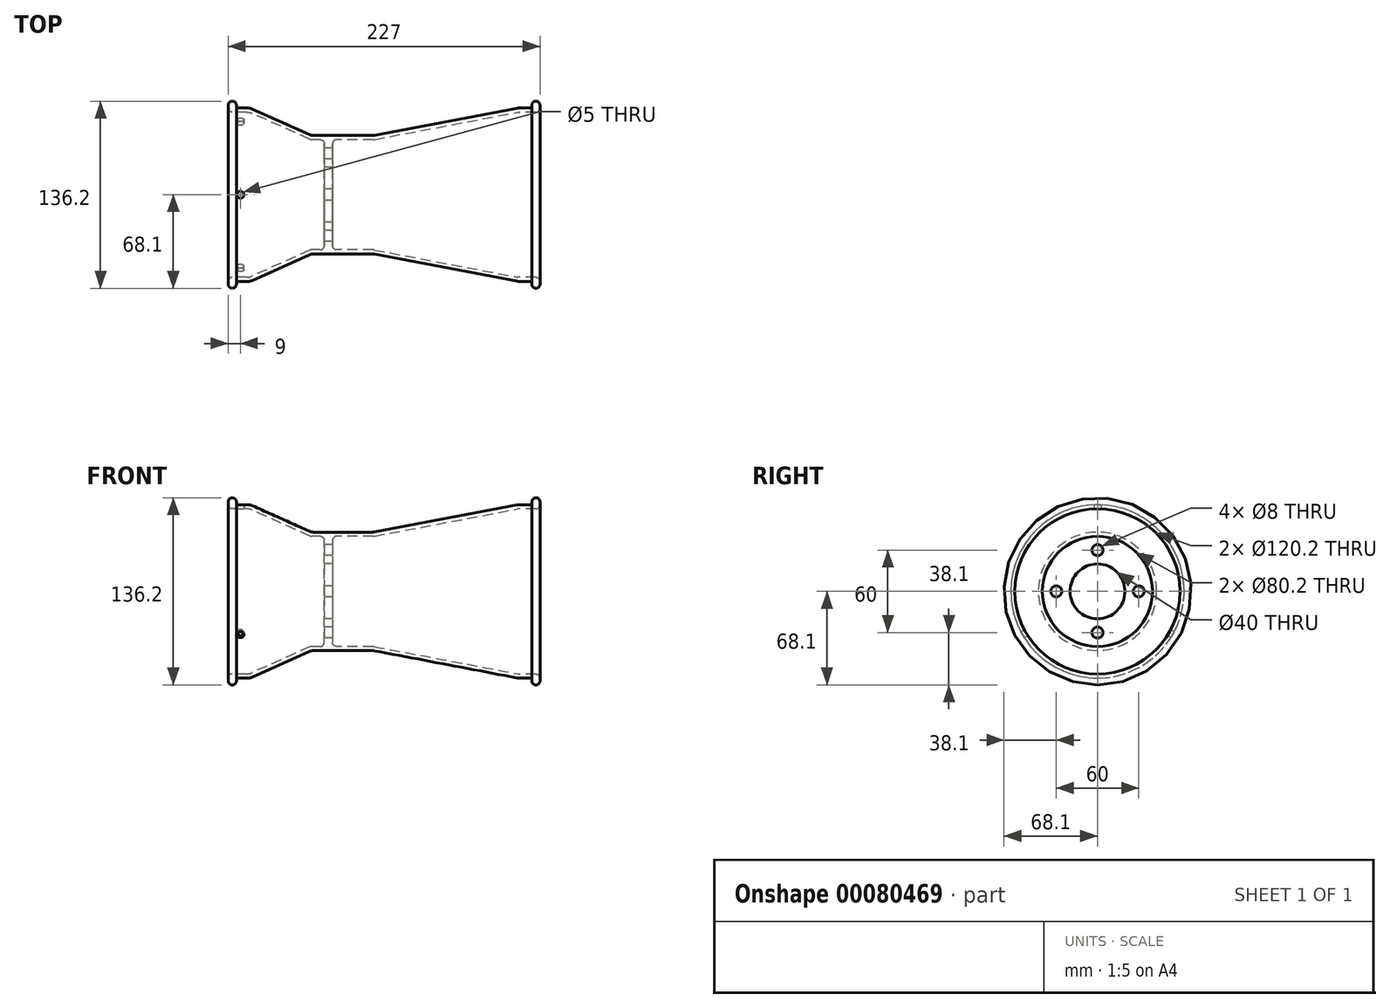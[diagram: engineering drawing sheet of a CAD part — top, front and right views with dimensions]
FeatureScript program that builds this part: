
annotation { "Feature Type Name" : "Feature", "Feature Type Description" : "" }
export const myFeature = defineFeature(function(context is Context, id is Id, definition is map)
    precondition{}
    {
        {
            var Q0;
            Q0=qCreatedBy(makeId("Front.planeOp"),FACE);
            var sketch = newSketch(context, id + "F0", { "sketchPlane" : qUnion([Q0])});
            skLineSegment(sketch, "E0", {"start": v(0, 0) * mm, "end": v(198.62, 0) * mm, "construction": true});
            skLineSegment(sketch, "E1", {"start": v(0, 68.1) * mm, "end": v(0, 60.1) * mm});
            skLineSegment(sketch, "E2", {"start": v(0, 60.1) * mm, "end": v(15.36, 60.1) * mm});
            skLineSegment(sketch, "E3", {"start": v(15.36, 60.1) * mm, "end": v(60, 40.1) * mm});
            skLineSegment(sketch, "E4", {"start": v(60, 40.1) * mm, "end": v(70, 40.1) * mm});
            skLineSegment(sketch, "E5", {"start": v(70, 40.1) * mm, "end": v(70, 0) * mm});
            skLineSegment(sketch, "E6", {"start": v(70, 0) * mm, "end": v(76, 0) * mm});
            skLineSegment(sketch, "E7", {"start": v(76, 0) * mm, "end": v(76, 40.1) * mm});
            skLineSegment(sketch, "E8", {"start": v(76, 40.1) * mm, "end": v(106, 40.1) * mm});
            skLineSegment(sketch, "E9", {"start": v(106, 40.1) * mm, "end": v(211.28, 60.1) * mm});
            skLineSegment(sketch, "E10", {"start": v(211.28, 60.1) * mm, "end": v(227, 60.1) * mm});
            skLineSegment(sketch, "E11", {"start": v(227, 60.1) * mm, "end": v(227, 68.1) * mm});
            skLineSegment(sketch, "E12", {"start": v(227, 68.1) * mm, "end": v(221, 68.1) * mm});
            skLineSegment(sketch, "E13", {"start": v(221, 68.1) * mm, "end": v(221, 63.1) * mm});
            skLineSegment(sketch, "E14", {"start": v(221, 63.1) * mm, "end": v(211, 63.1) * mm});
            skLineSegment(sketch, "E15", {"start": v(211, 63.1) * mm, "end": v(105.72, 43.1) * mm});
            skLineSegment(sketch, "E16", {"start": v(105.72, 43.1) * mm, "end": v(60.64, 43.1) * mm});
            skLineSegment(sketch, "E17", {"start": v(60.64, 43.1) * mm, "end": v(16, 63.1) * mm});
            skLineSegment(sketch, "E18", {"start": v(16, 63.1) * mm, "end": v(6, 63.1) * mm});
            skLineSegment(sketch, "E19", {"start": v(6, 63.1) * mm, "end": v(6, 68.1) * mm});
            skLineSegment(sketch, "E20", {"start": v(6, 68.1) * mm, "end": v(0, 68.1) * mm});
            skSolve(sketch);
        }
        {
            var Q0;
            Q0=makeQuery(id+"F0.imprint","IMPRINT",FACE,{"disambiguationData":[TD([[makeQuery(id+"F0.imprint","IMPRINT",EDGE,{"derivedFrom":sQuery(id+"F0.wireOp",EDGE,"E1")}),1.0]])]});
            var Q1;
            Q1=sQuery(id+"F0.wireOp",EDGE,"E0");
            revolve(context, id + "F1", {"entities" : qUnion([Q0]), "axis" : qUnion([Q1]), "revolveType" : RevolveType.FULL});
        }
        {
            var Q0;
            Q0=makeQuery(id+"F1.opRevolve","SWEPT_EDGE",EDGE,{"disambiguationData":[OSD([sQuery(id+"F0.wireOp",EDGE,"E17"),sQuery(id+"F0.wireOp",EDGE,"E18")])]});
            var Q1;
            Q1=makeQuery(id+"F1.opRevolve","SWEPT_EDGE",EDGE,{"disambiguationData":[OSD([sQuery(id+"F0.wireOp",EDGE,"E14"),sQuery(id+"F0.wireOp",EDGE,"E15")])]});
            var Q2;
            Q2=makeQuery(id+"F1.opRevolve","SWEPT_EDGE",EDGE,{"disambiguationData":[OSD([sQuery(id+"F0.wireOp",EDGE,"E15"),sQuery(id+"F0.wireOp",EDGE,"E16")])]});
            var Q3;
            Q3=makeQuery(id+"F1.opRevolve","SWEPT_EDGE",EDGE,{"disambiguationData":[OSD([sQuery(id+"F0.wireOp",EDGE,"E16"),sQuery(id+"F0.wireOp",EDGE,"E17")])]});
            var Q4;
            Q4=makeQuery(id+"F1.opRevolve","SWEPT_EDGE",EDGE,{"disambiguationData":[OSD([sQuery(id+"F0.wireOp",EDGE,"E2"),sQuery(id+"F0.wireOp",EDGE,"E3")])]});
            var Q5;
            Q5=makeQuery(id+"F1.opRevolve","SWEPT_EDGE",EDGE,{"disambiguationData":[OSD([sQuery(id+"F0.wireOp",EDGE,"E9"),sQuery(id+"F0.wireOp",EDGE,"E10")])]});
            fillet(context, id + "F2", {"entities" : qUnion([Q0, Q1, Q2, Q3, Q4, Q5]), "radius" : 8 * mm, "tangentPropagation" : true, "allowEdgeOverflow" : false});
        }
        {
            var Q0;
            Q0=makeQuery(id+"F1.opRevolve","SWEPT_EDGE",EDGE,{"disambiguationData":[OSD([sQuery(id+"F0.wireOp",EDGE,"E1"),sQuery(id+"F0.wireOp",EDGE,"E20")])]});
            var Q1;
            Q1=makeQuery(id+"F1.opRevolve","SWEPT_EDGE",EDGE,{"disambiguationData":[OSD([sQuery(id+"F0.wireOp",EDGE,"E19"),sQuery(id+"F0.wireOp",EDGE,"E20")])]});
            var Q2;
            Q2=makeQuery(id+"F1.opRevolve","SWEPT_EDGE",EDGE,{"disambiguationData":[OSD([sQuery(id+"F0.wireOp",EDGE,"E12"),sQuery(id+"F0.wireOp",EDGE,"E13")])]});
            var Q3;
            Q3=makeQuery(id+"F1.opRevolve","SWEPT_EDGE",EDGE,{"disambiguationData":[OSD([sQuery(id+"F0.wireOp",EDGE,"E11"),sQuery(id+"F0.wireOp",EDGE,"E12")])]});
            var Q4;
            Q4=makeQuery(id+"F1.opRevolve","SWEPT_EDGE",EDGE,{"disambiguationData":[OSD([sQuery(id+"F0.wireOp",EDGE,"E1"),sQuery(id+"F0.wireOp",EDGE,"E2")])]});
            var Q5;
            Q5=makeQuery(id+"F1.opRevolve","SWEPT_EDGE",EDGE,{"disambiguationData":[OSD([sQuery(id+"F0.wireOp",EDGE,"E3"),sQuery(id+"F0.wireOp",EDGE,"E4")])]});
            var Q6;
            Q6=makeQuery(id+"F1.opRevolve","SWEPT_EDGE",EDGE,{"disambiguationData":[OSD([sQuery(id+"F0.wireOp",EDGE,"E4"),sQuery(id+"F0.wireOp",EDGE,"E5")])]});
            var Q7;
            Q7=makeQuery(id+"F1.opRevolve","SWEPT_EDGE",EDGE,{"disambiguationData":[OSD([sQuery(id+"F0.wireOp",EDGE,"E10"),sQuery(id+"F0.wireOp",EDGE,"E11")])]});
            var Q8;
            Q8=makeQuery(id+"F1.opRevolve","SWEPT_EDGE",EDGE,{"disambiguationData":[OSD([sQuery(id+"F0.wireOp",EDGE,"E7"),sQuery(id+"F0.wireOp",EDGE,"E8")])]});
            var Q9;
            Q9=makeQuery(id+"F1.opRevolve","SWEPT_EDGE",EDGE,{"disambiguationData":[OSD([sQuery(id+"F0.wireOp",EDGE,"E8"),sQuery(id+"F0.wireOp",EDGE,"E9")])]});
            fillet(context, id + "F3", {"entities" : qUnion([Q0, Q1, Q2, Q3, Q4, Q5, Q6, Q7, Q8, Q9]), "radius" : 3 * mm, "tangentPropagation" : true, "allowEdgeOverflow" : false});
        }
        {
            var Q0;
            Q0=makeQuery(id+"F1.opRevolve","SWEPT_FACE",FACE,{"disambiguationData":[OSD([sQuery(id+"F0.wireOp",EDGE,"E5")])]});
            var sketch = newSketch(context, id + "F4", { "sketchPlane" : qUnion([Q0])});
            skCircle(sketch, "E21", {"center": v(0, 0) * mm, "radius": 30 * mm, "construction": true});
            skCircle(sketch, "E22", {"center": v(0, 30) * mm, "radius": 4 * mm});
            skCircle(sketch, "E23", {"center": v(30, 0) * mm, "radius": 4 * mm});
            skCircle(sketch, "E24", {"center": v(0, -30) * mm, "radius": 4 * mm});
            skCircle(sketch, "E25", {"center": v(-30, 0) * mm, "radius": 4 * mm});
            skCircle(sketch, "E26", {"center": v(0, 0) * mm, "radius": 20 * mm});
            skSolve(sketch);
        }
        {
            var Q0;
            Q0=qSketchRegion(id+"F4",true);
            extrude(context, id + "F5", {"entities" : qUnion([Q0]), "operationType" : NewBodyOperationType.REMOVE, "endBound" : BoundingType.THROUGH_ALL, "oppositeDirection" : true, "depth" : 25 * mm});
        }
        {
            var Q0;
            Q0=qCreatedBy(makeId("Top.planeOp"),FACE);
            var sketch = newSketch(context, id + "F6", { "sketchPlane" : qUnion([Q0])});
            skCircle(sketch, "E27", {"center": v(9, 0) * mm, "radius": 2.5 * mm});
            skSolve(sketch);
        }
        {
            var Q0;
            Q0=qSketchRegion(id+"F6",true);
            extrude(context, id + "F7", {"entities" : qUnion([Q0]), "operationType" : NewBodyOperationType.REMOVE, "endBound" : BoundingType.THROUGH_ALL, "depth" : 25 * mm});
        }
        {
            var Q0;
            Q0=makeQuery(id+"F7.boolean.opBoolean","COPY",FACE,{"derivedFrom":makeQuery(id+"F7.opExtrude","SWEPT_FACE",FACE,{"disambiguationData":[OSD([sQuery(id+"F6.wireOp",EDGE,"E27")])]})});
            var Q1;
            Q1=makeQuery(id+"F5.boolean.opBoolean","COPY",FACE,{"derivedFrom":makeQuery(id+"F5.opExtrude","SWEPT_FACE",FACE,{"disambiguationData":[OSD([sQuery(id+"F4.wireOp",EDGE,"E26")])]})});
            circularPattern(context, id + "F8", {"faces" : qUnion([Q0]), "axis" : qUnion([Q1]), "angle" : 360 * degree, "instanceCount" : 3, "equalSpace" : true, "patternType" : PatternType.FACE, "computeTransformsWithoutBuiltin" : true});
        }
    });
